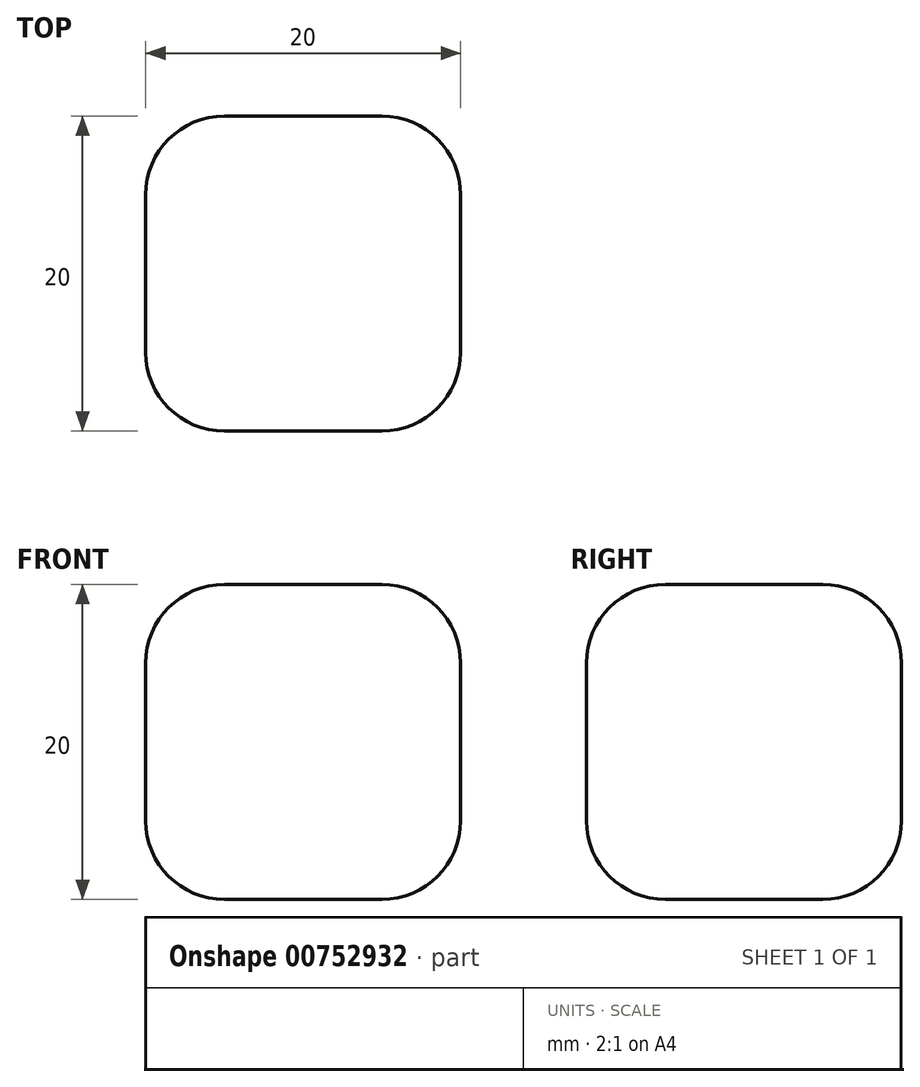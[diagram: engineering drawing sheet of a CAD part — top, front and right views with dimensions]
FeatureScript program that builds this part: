
annotation { "Feature Type Name" : "Feature", "Feature Type Description" : "" }
export const myFeature = defineFeature(function(context is Context, id is Id, definition is map)
    precondition{}
    {
        {
            var Q0;
            Q0=qCreatedBy(makeId("Top.planeOp"),FACE);
            var sketch = newSketch(context, id + "F0", { "sketchPlane" : qUnion([Q0])});
            skLineSegment(sketch, "E0.bottom", {"start": v(-20, 0) * mm, "end": v(0, 0) * mm});
            skLineSegment(sketch, "E0.top", {"start": v(-20, -20) * mm, "end": v(0, -20) * mm});
            skLineSegment(sketch, "E0.left", {"start": v(-20, 0) * mm, "end": v(-20, -20) * mm});
            skLineSegment(sketch, "E0.right", {"start": v(0, 0) * mm, "end": v(0, -20) * mm});
            skSolve(sketch);
        }
        {
            var Q0;
            Q0=makeQuery(id+"F0.imprint","IMPRINT",FACE,{"disambiguationData":[TD([[makeQuery(id+"F0.imprint","IMPRINT",EDGE,{"derivedFrom":sQuery(id+"F0.wireOp",EDGE,"E0.bottom")}),-1.0]])]});
            extrude(context, id + "F1", {"entities" : qUnion([Q0]), "depth" : 20 * mm, "offsetDistance" : 25 * mm});
        }
        {
            var Q0;
            Q0=makeQuery(id+"F1.opExtrude","CAP_EDGE",EDGE,{"disambiguationData":[OSD([sQuery(id+"F0.wireOp",EDGE,"E0.top")])],"isStart":true});
            var Q1;
            Q1=makeQuery(id+"F1.opExtrude","CAP_EDGE",EDGE,{"disambiguationData":[OSD([sQuery(id+"F0.wireOp",EDGE,"E0.left")])],"isStart":true});
            var Q2;
            Q2=makeQuery(id+"F1.opExtrude","CAP_EDGE",EDGE,{"disambiguationData":[OSD([sQuery(id+"F0.wireOp",EDGE,"E0.bottom")])],"isStart":true});
            var Q3;
            Q3=makeQuery(id+"F1.opExtrude","CAP_EDGE",EDGE,{"disambiguationData":[OSD([sQuery(id+"F0.wireOp",EDGE,"E0.right")])],"isStart":true});
            var Q4;
            Q4=makeQuery(id+"F1.opExtrude","CAP_EDGE",EDGE,{"disambiguationData":[OSD([sQuery(id+"F0.wireOp",EDGE,"E0.top")])],"isStart":false});
            var Q5;
            Q5=makeQuery(id+"F1.opExtrude","CAP_EDGE",EDGE,{"disambiguationData":[OSD([sQuery(id+"F0.wireOp",EDGE,"E0.right")])],"isStart":false});
            var Q6;
            Q6=makeQuery(id+"F1.opExtrude","CAP_EDGE",EDGE,{"disambiguationData":[OSD([sQuery(id+"F0.wireOp",EDGE,"E0.bottom")])],"isStart":false});
            var Q7;
            Q7=makeQuery(id+"F1.opExtrude","CAP_EDGE",EDGE,{"disambiguationData":[OSD([sQuery(id+"F0.wireOp",EDGE,"E0.left")])],"isStart":false});
            var Q8;
            Q8=makeQuery(id+"F1.opExtrude","SWEPT_EDGE",EDGE,{"disambiguationData":[OSD([sQuery(id+"F0.wireOp",EDGE,"E0.bottom"),sQuery(id+"F0.wireOp",EDGE,"E0.left")])]});
            var Q9;
            Q9=makeQuery(id+"F1.opExtrude","SWEPT_EDGE",EDGE,{"disambiguationData":[OSD([sQuery(id+"F0.wireOp",EDGE,"E0.bottom"),sQuery(id+"F0.wireOp",EDGE,"E0.right")])]});
            var Q10;
            Q10=makeQuery(id+"F1.opExtrude","SWEPT_EDGE",EDGE,{"disambiguationData":[OSD([sQuery(id+"F0.wireOp",EDGE,"E0.top"),sQuery(id+"F0.wireOp",EDGE,"E0.right")])]});
            var Q11;
            Q11=makeQuery(id+"F1.opExtrude","SWEPT_EDGE",EDGE,{"disambiguationData":[OSD([sQuery(id+"F0.wireOp",EDGE,"E0.top"),sQuery(id+"F0.wireOp",EDGE,"E0.left")])]});
            fillet(context, id + "F2", {"entities" : qUnion([Q0, Q1, Q2, Q3, Q4, Q5, Q6, Q7, Q8, Q9, Q10, Q11]), "radius" : 5 * mm, "tangentPropagation" : true, "allowEdgeOverflow" : false});
        }
    });
